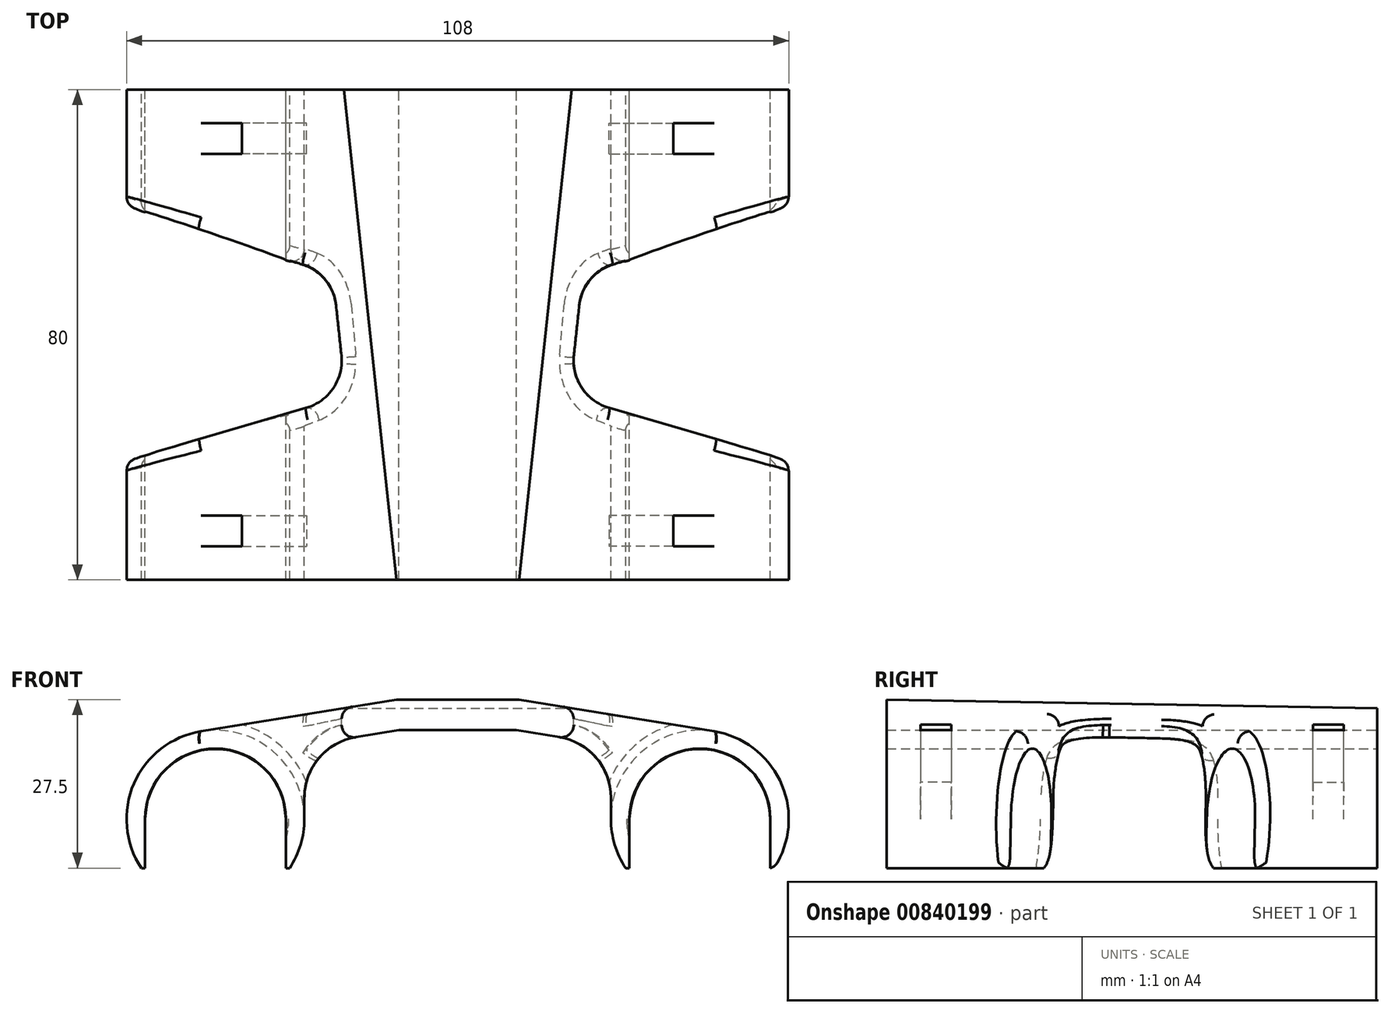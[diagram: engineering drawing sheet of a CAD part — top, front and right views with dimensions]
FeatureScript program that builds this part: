
annotation { "Feature Type Name" : "Feature", "Feature Type Description" : "" }
export const myFeature = defineFeature(function(context is Context, id is Id, definition is map)
    precondition{}
    {
        {
            var Q0;
            Q0=qCreatedBy(makeId("Front.planeOp"),FACE);
            var sketch = newSketch(context, id + "F0", { "sketchPlane" : qUnion([Q0])});
            skArc(sketch, "E0", {"start": v(51, 0) * mm, "mid": v(39.5, 11.5) * mm, "end": v(28, 0) * mm});
            skLineSegment(sketch, "E1", {"start": v(0, 0) * mm, "end": v(39.5, 0) * mm, "construction": true});
            skArc(sketch, "E2.0", {"start": v(51.6, -8) * mm, "mid": v(52.78, 5.81) * mm, "end": v(41.83, 14.31) * mm});
            skLineSegment(sketch, "E3", {"start": v(0, 19.5) * mm, "end": v(10, 19.5) * mm});
            skLineSegment(sketch, "E4", {"start": v(10, 19.5) * mm, "end": v(41.83, 14.31) * mm});
            skLineSegment(sketch, "E5.0", {"start": v(9.6, 14.5) * mm, "end": v(16.6, 13.36) * mm});
            skLineSegment(sketch, "E5.1", {"start": v(0, 14.5) * mm, "end": v(9.6, 14.5) * mm});
            skLineSegment(sketch, "E6", {"start": v(25, 0) * mm, "end": v(25, 3.49) * mm});
            skPoint(sketch, "E7.visualSharp", {"position": v(25, 11.99) * mm});
            skArc(sketch, "E7.filletArc", {"start": v(25, 3.49) * mm, "mid": v(22.62, 9.96) * mm, "end": v(16.6, 13.36) * mm});
            skLineSegment(sketch, "E8", {"start": v(27.4, -8) * mm, "end": v(28, -8) * mm});
            skLineSegment(sketch, "E9", {"start": v(28, 0) * mm, "end": v(28, -8) * mm});
            skLineSegment(sketch, "E10", {"start": v(51, 0) * mm, "end": v(51, -8) * mm});
            skLineSegment(sketch, "E11.trimOffspring", {"start": v(51, -8) * mm, "end": v(51.6, -8) * mm});
            skArc(sketch, "E12.trimOffspring", {"start": v(25, 0) * mm, "mid": v(25.61, -4.18) * mm, "end": v(27.4, -8) * mm});
            skLineSegment(sketch, "E13", {"start": v(0, 19.5) * mm, "end": v(0, 14.5) * mm});
            skSolve(sketch);
        }
        {
            var Q0;
            Q0 = qSketchRegion(id + "F0", true);
            extrude(context, id + "F1", {"entities" : qUnion([Q0]), "endBound" : BoundingType.SYMMETRIC, "depth" : 80 * mm, "offsetDistance" : 25 * mm});
        }
        {
            var Q0;
            Q0=makeQuery(id+"F1.opExtrude","CAP_EDGE",EDGE,{"disambiguationData":[OSD([sQuery(id+"F0.wireOp",EDGE,"E3")])],"isStart":true});
            chamfer(context, id + "F2", {"entities" : qUnion([Q0]), "chamferType" : ChamferType.OFFSET_ANGLE, "width" : 80 * mm, "oppositeDirection" : true, "angle" : 1 * degree, "tangentPropagation" : true});
        }
        {
            var Q0;
            Q0=makeQuery(id+"F2.opChamfer","BLEND_FACE",FACE,{"disambiguationData":[OSD([sQuery(id+"F0.wireOp",EDGE,"E3")])]});
            var sketch = newSketch(context, id + "F3", { "sketchPlane" : qUnion([Q0])});
            skLineSegment(sketch, "E14", {"start": v(55, 21.42) * mm, "end": v(20.37, 9.57) * mm});
            skLineSegment(sketch, "E15", {"start": v(18.24, -10.33) * mm, "end": v(55, -20.95) * mm});
            skLineSegment(sketch, "E16", {"start": v(55, -20.95) * mm, "end": v(55, 21.42) * mm});
            skLineSegment(sketch, "E17", {"start": v(18.24, -10.33) * mm, "end": v(20.37, 9.57) * mm});
            skPoint(sketch, "E18.orphan", {"position": v(16.63, 8.3) * mm});
            skSolve(sketch);
        }
        {
            var Q0;
            Q0=makeQuery(id+"F3.imprint","IMPRINT",FACE,{"disambiguationData":[TD([[makeQuery(id+"F3.imprint","IMPRINT",EDGE,{"derivedFrom":sQuery(id+"F3.wireOp",EDGE,"E14")}),1.0]])]});
            extrude(context, id + "F4", {"entities" : qUnion([Q0]), "operationType" : NewBodyOperationType.REMOVE, "endBound" : BoundingType.THROUGH_ALL, "oppositeDirection" : true, "depth" : 25 * mm, "offsetDistance" : 25 * mm});
        }
        {
            var Q0;
            Q0=makeQuery(id+"F4.boolean.opBoolean","COPY",EDGE,{"derivedFrom":makeQuery(id+"F4.opExtrude","SWEPT_EDGE",EDGE,{"disambiguationData":[OSD([sQuery(id+"F3.wireOp",EDGE,"E14"),sQuery(id+"F3.wireOp",EDGE,"E17")])]})});
            var Q1;
            Q1=makeQuery(id+"F4.boolean.opBoolean","COPY",EDGE,{"derivedFrom":makeQuery(id+"F4.opExtrude","SWEPT_EDGE",EDGE,{"disambiguationData":[OSD([sQuery(id+"F3.wireOp",EDGE,"E15"),sQuery(id+"F3.wireOp",EDGE,"E17")])]})});
            fillet(context, id + "F5", {"entities" : qUnion([Q0, Q1]), "radius" : 8 * mm, "tangentPropagation" : true, "allowEdgeOverflow" : false});
        }
        {
            var Q0;
            {var subQ0=makeQuery(id+"F1.opExtrude","CAP_FACE",FACE,{"disambiguationData":[OSD([sQuery(id+"F0.wireOp",EDGE,"E0"),sQuery(id+"F0.wireOp",EDGE,"E2.0"),sQuery(id+"F0.wireOp",EDGE,"E3"),sQuery(id+"F0.wireOp",EDGE,"E4"),sQuery(id+"F0.wireOp",EDGE,"E5.0"),sQuery(id+"F0.wireOp",EDGE,"E5.1"),sQuery(id+"F0.wireOp",EDGE,"E6"),sQuery(id+"F0.wireOp",EDGE,"E7.filletArc"),sQuery(id+"F0.wireOp",EDGE,"E8"),sQuery(id+"F0.wireOp",EDGE,"E9"),sQuery(id+"F0.wireOp",EDGE,"E10"),sQuery(id+"F0.wireOp",EDGE,"E11.trimOffspring"),sQuery(id+"F0.wireOp",EDGE,"E12.trimOffspring"),sQuery(id+"F0.wireOp",EDGE,"E13")])],"isStart":false});Q0=makeQuery(id+"FHFeFmnZixUwJ2z_1.boolean.opBoolean","MERGE",FACE,{"derivedFrom":[subQ0,makeQuery(id+"FHFeFmnZixUwJ2z_1.opPattern","COPY",FACE,{"derivedFrom":subQ0,"instanceName":"1"})]});}
            cPlane(context, id + "F6", {"entities" : qUnion([Q0]), "cplaneType" : CPlaneType.OFFSET, "offset" : 8 * mm, "oppositeDirection" : true, "width" : 150 * mm, "height" : 150 * mm});
        }
        {
            var Q0;
            {var subQ0=makeQuery(id+"F1.opExtrude","CAP_FACE",FACE,{"disambiguationData":[OSD([sQuery(id+"F0.wireOp",EDGE,"E0"),sQuery(id+"F0.wireOp",EDGE,"E2.0"),sQuery(id+"F0.wireOp",EDGE,"E3"),sQuery(id+"F0.wireOp",EDGE,"E4"),sQuery(id+"F0.wireOp",EDGE,"E5.0"),sQuery(id+"F0.wireOp",EDGE,"E5.1"),sQuery(id+"F0.wireOp",EDGE,"E6"),sQuery(id+"F0.wireOp",EDGE,"E7.filletArc"),sQuery(id+"F0.wireOp",EDGE,"E8"),sQuery(id+"F0.wireOp",EDGE,"E9"),sQuery(id+"F0.wireOp",EDGE,"E10"),sQuery(id+"F0.wireOp",EDGE,"E11.trimOffspring"),sQuery(id+"F0.wireOp",EDGE,"E12.trimOffspring"),sQuery(id+"F0.wireOp",EDGE,"E13")])],"isStart":true});Q0=makeQuery(id+"FHFeFmnZixUwJ2z_1.boolean.opBoolean","MERGE",FACE,{"derivedFrom":[subQ0,makeQuery(id+"FHFeFmnZixUwJ2z_1.opPattern","COPY",FACE,{"derivedFrom":subQ0,"instanceName":"1"})]});}
            cPlane(context, id + "F7", {"entities" : qUnion([Q0]), "cplaneType" : CPlaneType.OFFSET, "offset" : 8 * mm, "oppositeDirection" : true, "width" : 150 * mm, "height" : 150 * mm});
        }
        {
            var Q0;
            Q0=qCreatedBy(id+"F6.planeOp",FACE);
            var sketch = newSketch(context, id + "F8", { "sketchPlane" : qUnion([Q0])});
            skArc(sketch, "E19.converted", {"start": v(41.83, 14.31) * mm, "mid": v(30.1, 11.05) * mm, "end": v(25, 0) * mm});
            skPoint(sketch, "E20.orphan", {"position": v(41.83, 14.31) * mm});
            skArc(sketch, "E21.0", {"start": v(35.16, 15.4) * mm, "mid": v(28.83, 11.92) * mm, "end": v(24.67, 6.02) * mm});
            skArc(sketch, "E22.0", {"start": v(25, 3.49) * mm, "mid": v(24.92, 4.76) * mm, "end": v(24.67, 6.02) * mm});
            skLineSegment(sketch, "E23.0", {"start": v(25, 0) * mm, "end": v(25, 3.49) * mm});
            skLineSegment(sketch, "E24.0", {"start": v(35.16, 15.4) * mm, "end": v(41.83, 14.31) * mm});
            skPoint(sketch, "E25.orphan", {"position": v(16.6, 13.36) * mm});
            skPoint(sketch, "E26.orphan", {"position": v(10, 19.5) * mm});
            skSolve(sketch);
        }
        {
            var Q0;
            Q0 = qSketchRegion(id + "F8", true);
            extrude(context, id + "F9", {"entities" : qUnion([Q0]), "operationType" : NewBodyOperationType.REMOVE, "endBound" : BoundingType.SYMMETRIC, "oppositeDirection" : true, "depth" : 5 * mm, "offsetDistance" : 25 * mm});
        }
        {
            var Q0;
            Q0=qCreatedBy(id+"F7.planeOp",FACE);
            var sketch = newSketch(context, id + "F10", { "sketchPlane" : qUnion([Q0])});
            skArc(sketch, "E27.converted", {"start": v(-41.83, 14.31) * mm, "mid": v(-30.1, 11.05) * mm, "end": v(-25, 0) * mm});
            skPoint(sketch, "E28.orphan", {"position": v(-41.83, 14.31) * mm});
            skLineSegment(sketch, "E29.0", {"start": v(-35.16, 15.4) * mm, "end": v(-41.83, 14.31) * mm});
            skLineSegment(sketch, "E30.0", {"start": v(-25, 0) * mm, "end": v(-25, 3.49) * mm});
            skArc(sketch, "E31.0", {"start": v(-25, 3.49) * mm, "mid": v(-24.92, 4.76) * mm, "end": v(-24.67, 6.02) * mm});
            skArc(sketch, "E32.0", {"start": v(-35.16, 15.4) * mm, "mid": v(-28.83, 11.92) * mm, "end": v(-24.67, 6.02) * mm});
            skPoint(sketch, "E33.orphan", {"position": v(-18.57, 18.1) * mm});
            skPoint(sketch, "E34.orphan", {"position": v(-16.6, 13.36) * mm});
            skSolve(sketch);
        }
        {
            var Q0;
            Q0 = qSketchRegion(id + "F10", true);
            extrude(context, id + "F11", {"entities" : qUnion([Q0]), "operationType" : NewBodyOperationType.REMOVE, "endBound" : BoundingType.SYMMETRIC, "oppositeDirection" : true, "depth" : 5 * mm, "offsetDistance" : 25 * mm});
        }
        {
            var Q0;
            Q0=makeQuery(id+"F1.opExtrude","SWEPT_BODY",BODY,{"disambiguationData":[OSD([sQuery(id+"F0.wireOp",EDGE,"E0"),sQuery(id+"F0.wireOp",EDGE,"E2.0"),sQuery(id+"F0.wireOp",EDGE,"E3"),sQuery(id+"F0.wireOp",EDGE,"E4"),sQuery(id+"F0.wireOp",EDGE,"E5.0"),sQuery(id+"F0.wireOp",EDGE,"E5.1"),sQuery(id+"F0.wireOp",EDGE,"E6"),sQuery(id+"F0.wireOp",EDGE,"E7.filletArc"),sQuery(id+"F0.wireOp",EDGE,"E8"),sQuery(id+"F0.wireOp",EDGE,"E9"),sQuery(id+"F0.wireOp",EDGE,"E10"),sQuery(id+"F0.wireOp",EDGE,"E11.trimOffspring"),sQuery(id+"F0.wireOp",EDGE,"E12.trimOffspring"),sQuery(id+"F0.wireOp",EDGE,"E13")])]});
            var Q1;
            Q1=makeQuery(id+"F1.opExtrude","SWEPT_FACE",FACE,{"disambiguationData":[OSD([sQuery(id+"F0.wireOp",EDGE,"E13")])]});
            mirror(context, id + "F12", {"operationType" : NewBodyOperationType.ADD, "entities" : qUnion([Q0]), "mirrorPlane" : qUnion([Q1])});
        }
        {
            var Q0;
            Q0=makeQuery(id+"F4.boolean.opBoolean","INTERSECT",EDGE,{"derivedFrom":[makeQuery(id+"F1.opExtrude","SWEPT_FACE",FACE,{"disambiguationData":[OSD([sQuery(id+"F0.wireOp",EDGE,"E4")])]}),makeQuery(id+"F4.opExtrude","SWEPT_FACE",FACE,{"disambiguationData":[OSD([sQuery(id+"F3.wireOp",EDGE,"E17")])]})]});
            var Q1;
            Q1=makeQuery(id+"F12.opPattern","COPY",EDGE,{"derivedFrom":makeQuery(id+"F4.boolean.opBoolean","INTERSECT",EDGE,{"derivedFrom":[makeQuery(id+"F1.opExtrude","SWEPT_FACE",FACE,{"disambiguationData":[OSD([sQuery(id+"F0.wireOp",EDGE,"E4")])]}),makeQuery(id+"F4.opExtrude","SWEPT_FACE",FACE,{"disambiguationData":[OSD([sQuery(id+"F3.wireOp",EDGE,"E17")])]})]}),"instanceName":"1"});
            var Q2;
            {var subQ0=sQuery(id+"F0.wireOp",EDGE,"E11.trimOffspring");var subQ1=sQuery(id+"F0.wireOp",EDGE,"E2.0");Q2=makeQuery(id+"F4.boolean.opBoolean","SPLIT",EDGE,{"disambiguationData":[TD([makeQuery(id+"F4.opExtrude","SWEPT_FACE",FACE,{"disambiguationData":[OSD([sQuery(id+"F3.wireOp",EDGE,"E15")])]})])],"derivedFrom":makeQuery(id+"F1.opExtrude","SWEPT_EDGE",EDGE,{"disambiguationData":[OSD([subQ1,subQ0])]})});}
            var Q3;
            {var subQ0=sQuery(id+"F0.wireOp",EDGE,"E11.trimOffspring");var subQ1=sQuery(id+"F0.wireOp",EDGE,"E2.0");Q3=makeQuery(id+"F4.boolean.opBoolean","SPLIT",EDGE,{"disambiguationData":[TD([makeQuery(id+"F4.opExtrude","SWEPT_FACE",FACE,{"disambiguationData":[OSD([sQuery(id+"F3.wireOp",EDGE,"E14")])]})])],"derivedFrom":makeQuery(id+"F1.opExtrude","SWEPT_EDGE",EDGE,{"disambiguationData":[OSD([subQ1,subQ0])]})});}
            var Q4;
            Q4=makeQuery(id+"F4.boolean.opBoolean","INTERSECT",EDGE,{"derivedFrom":[makeQuery(id+"F1.opExtrude","SWEPT_FACE",FACE,{"disambiguationData":[OSD([sQuery(id+"F0.wireOp",EDGE,"E7.filletArc")])]}),makeQuery(id+"F4.opExtrude","SWEPT_FACE",FACE,{"disambiguationData":[OSD([sQuery(id+"F3.wireOp",EDGE,"E17")])]})]});
            var Q5;
            Q5=makeQuery(id+"F4.boolean.opBoolean","INTERSECT",EDGE,{"derivedFrom":[makeQuery(id+"F1.opExtrude","SWEPT_FACE",FACE,{"disambiguationData":[OSD([sQuery(id+"F0.wireOp",EDGE,"E12.trimOffspring")])]}),makeQuery(id+"F4.opExtrude","SWEPT_FACE",FACE,{"disambiguationData":[OSD([sQuery(id+"F3.wireOp",EDGE,"E14")])]})]});
            var Q6;
            Q6=makeQuery(id+"F4.boolean.opBoolean","INTERSECT",EDGE,{"derivedFrom":[makeQuery(id+"F1.opExtrude","SWEPT_FACE",FACE,{"disambiguationData":[OSD([sQuery(id+"F0.wireOp",EDGE,"E6")])]}),makeQuery(id+"F4.opExtrude","SWEPT_FACE",FACE,{"disambiguationData":[OSD([sQuery(id+"F3.wireOp",EDGE,"E14")])]})]});
            var Q7;
            Q7=makeQuery(id+"F4.boolean.opBoolean","INTERSECT",EDGE,{"derivedFrom":[makeQuery(id+"F1.opExtrude","SWEPT_FACE",FACE,{"disambiguationData":[OSD([sQuery(id+"F0.wireOp",EDGE,"E7.filletArc")])]}),makeQuery(id+"F4.opExtrude","SWEPT_FACE",FACE,{"disambiguationData":[OSD([sQuery(id+"F3.wireOp",EDGE,"E14")])]})]});
            var Q8;
            Q8=makeQuery(id+"F5.opFillet","BLEND_EDGE",EDGE,{"blendedFrom":[makeQuery(id+"F4.boolean.opBoolean","COPY",EDGE,{"derivedFrom":makeQuery(id+"F4.opExtrude","SWEPT_EDGE",EDGE,{"disambiguationData":[OSD([sQuery(id+"F3.wireOp",EDGE,"E14"),sQuery(id+"F3.wireOp",EDGE,"E17")])]})}),makeQuery(id+"F1.opExtrude","SWEPT_FACE",FACE,{"disambiguationData":[OSD([sQuery(id+"F0.wireOp",EDGE,"E7.filletArc")])]})],"blendedInto":[makeQuery(id+"F1.opExtrude","SWEPT_FACE",FACE,{"disambiguationData":[OSD([sQuery(id+"F0.wireOp",EDGE,"E7.filletArc")])]})]});
            var Q9;
            Q9=makeQuery(id+"F5.opFillet","BLEND_EDGE",EDGE,{"blendedFrom":[makeQuery(id+"F4.boolean.opBoolean","COPY",EDGE,{"derivedFrom":makeQuery(id+"F4.opExtrude","SWEPT_EDGE",EDGE,{"disambiguationData":[OSD([sQuery(id+"F3.wireOp",EDGE,"E15"),sQuery(id+"F3.wireOp",EDGE,"E17")])]})}),makeQuery(id+"F1.opExtrude","SWEPT_FACE",FACE,{"disambiguationData":[OSD([sQuery(id+"F0.wireOp",EDGE,"E7.filletArc")])]})],"blendedInto":[makeQuery(id+"F1.opExtrude","SWEPT_FACE",FACE,{"disambiguationData":[OSD([sQuery(id+"F0.wireOp",EDGE,"E7.filletArc")])]})]});
            var Q10;
            Q10=makeQuery(id+"F4.boolean.opBoolean","INTERSECT",EDGE,{"derivedFrom":[makeQuery(id+"F1.opExtrude","SWEPT_FACE",FACE,{"disambiguationData":[OSD([sQuery(id+"F0.wireOp",EDGE,"E7.filletArc")])]}),makeQuery(id+"F4.opExtrude","SWEPT_FACE",FACE,{"disambiguationData":[OSD([sQuery(id+"F3.wireOp",EDGE,"E15")])]})]});
            var Q11;
            Q11=makeQuery(id+"F4.boolean.opBoolean","INTERSECT",EDGE,{"derivedFrom":[makeQuery(id+"F1.opExtrude","SWEPT_FACE",FACE,{"disambiguationData":[OSD([sQuery(id+"F0.wireOp",EDGE,"E6")])]}),makeQuery(id+"F4.opExtrude","SWEPT_FACE",FACE,{"disambiguationData":[OSD([sQuery(id+"F3.wireOp",EDGE,"E15")])]})]});
            var Q12;
            Q12=makeQuery(id+"F4.boolean.opBoolean","INTERSECT",EDGE,{"derivedFrom":[makeQuery(id+"F1.opExtrude","SWEPT_FACE",FACE,{"disambiguationData":[OSD([sQuery(id+"F0.wireOp",EDGE,"E12.trimOffspring")])]}),makeQuery(id+"F4.opExtrude","SWEPT_FACE",FACE,{"disambiguationData":[OSD([sQuery(id+"F3.wireOp",EDGE,"E15")])]})]});
            var Q13;
            Q13=makeQuery(id+"F12.opPattern","COPY",EDGE,{"derivedFrom":makeQuery(id+"F4.boolean.opBoolean","INTERSECT",EDGE,{"derivedFrom":[makeQuery(id+"F1.opExtrude","SWEPT_FACE",FACE,{"disambiguationData":[OSD([sQuery(id+"F0.wireOp",EDGE,"E7.filletArc")])]}),makeQuery(id+"F4.opExtrude","SWEPT_FACE",FACE,{"disambiguationData":[OSD([sQuery(id+"F3.wireOp",EDGE,"E17")])]})]}),"instanceName":"1"});
            fillet(context, id + "F13", {"entities" : qUnion([Q0, Q1, Q2, Q3, Q4, Q5, Q6, Q7, Q8, Q9, Q10, Q11, Q12, Q13]), "radius" : 2 * mm, "tangentPropagation" : true, "allowEdgeOverflow" : false});
        }
    });
